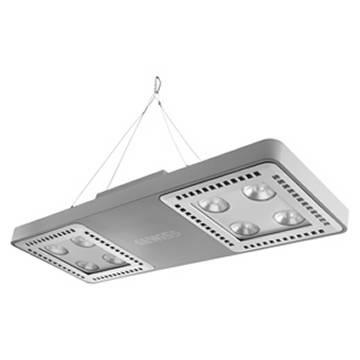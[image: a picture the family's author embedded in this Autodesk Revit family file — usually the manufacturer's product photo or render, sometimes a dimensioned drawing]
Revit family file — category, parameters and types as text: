
# Revit family: Lighting-Industriale-GEWISS-SMART[4]HE_APPARECCHI-LED_2M_DALI
name_source: partatom
category: Apparecchi per illuminazione
units: mm (PartAtom-declared; Revit-internal decimal feet)

## family parameters
Basato su piano di lavoro = Sì
Condiviso = No
Numero OmniClass = 23.80.70.00
Punto di calcolo locali = No
Quota connettore circolare = Usa diametro
Sempre verticale = No
Sorgente d'illuminazione = No
Taglio con vuoti quando caricato = No
Tipo di parte = Normale
Titolo OmniClass = Lighting

## types (1)
- Lighting-Industriale-GEWISS-SMART[4]HE_APPARECCHI-LED_2M_DALI
    Alimentatore = Incluso
    Apparecchio a ridotta temperatura superficiale = Si
    Applicazione = Interno
    Cablaggio = Con connettore stagno Gw connect
    Caratteristiche elettriche e gestione della luce = -
    Caratteristiche ottiche e illuminotecniche = -
    Carico apparente = 97 VA
    Catalogo = LIGHTING
    Certificazione DIN 18032-3 = Con Staffa - Kit Funi + morsetto (in approvazione)
    Certificazioni e classificazioni = -
    Classe fotobiologica = RG0
    Classe isolamento = I
    Classificazione = Lighting
    Classificazione: = -
    Codice Electrocod = 2444
    Codice digitale univoco (Datamatrix) = Datamatrix
    Colore = Grigio RAL 7035
    Commenti sul wattaggio = 97W
    Contesto = Illuminazione di industrie e impianti sportivi
    Controllo abbagliamento e luminanza = -
    Corpo = PA6 “Halogen Free” caricato fibra vetro
    Descrizione = SMART[4]HB 2M C.PAS.DALI ELL.57K
    Dispositivo di protezione = DM 6 kV / CM 10 kV
    Dist_sorg_lum = 10 mm  [stored 0.0328084 ft]
    Durata di vita = L90B10 (Tq+25°C) = 100.000 h - L90B10 (Tq+50°C) = 50.000 h
    Efficienza luminosa (lm/W) = 129
    Finitura colore = Grigio RAL 7035
    Fissaggio = -
    Frequenza nominale (Hz) = 50/60 Hz
    Gancio di chiusura = -
    Garanzia = 5 anni
    Grado di protezione = IP66
    Gruppo ottico = Riflettore in PC metallizzato e lenti in PMMA
    Guarnizioni = tipo siliconico antinvecchiamento
    IDF = ccb2858a-98df-48b0-bf72-33839f1a2588
    IDT = 32167967fdf74962832821affbd5ec12
    IPEA = -
    Immagine tipo = GWL1311.jpg
    Inclinazione = Con accessorio staffa
    Indice di resa cromatica = CRI-80
    Informazioni generali = -
    Installazione e manutenzione = -
    Lampada = LED
    Larghezza = 254 mm
    Lumen output (lm) = 12300
    Lunghezza = 699 mm  [stored 2.29331 ft]
    Mascherina = <Per categoria>
    Materiali = -
    Modello = GWS4223AQ857
    Motore = <Per categoria>
    Norma di riferimento = EN 60598-1 ; EN 60598-2-1 ; EN 60598-2-24
    Ottica = Ellittica
    Peso (kg): = 6,5
    Potenza di sistema = 95W
    Produttore = GEWISS S.p.A.
    Prospetto di default = 1219 mm
    Resistenza agli urti = IK08
    Resistenza al filo incandescente = 850 °C
    SEO = High bay
    Scheda Tecnica = https://www.gewiss.com
    Schermo = Vetro Temprato Spessore 4mm
    Sistema di controllo = 1 x DALI DT6
    Sistema di controllo : = DALI
    Sostituibilità gruppo ottico = Non sostituibile
    Sostituibilità piastra di cablaggio = Non sostituibile
    Spessore plafoniera = 40 mm  [stored 0.131234 ft]
    Struttura plafoniera = <Per categoria>
    Superficie massima esposta al vento : = 0,184 m²
    Temperatura di colore = 5700K
    Temperatura di esercizio = -30°C ÷ +50 °C
    Temperatura di stoccaggio = -40 +70 °C
    Tensione di alimentazione = 220 - 240 V
    Tipo di apparecchio = Riflettore industriale a LED&nbsp;
    Tipo di installazione e montaggio = Plafone - Parete - Sospensione
    Tipologia sorgente luminosa = LED - Non sostituibile
    Tolleranza cromatica = SDCM = 3
    Trasformatore = <Per categoria>
    URL = https://www.gewiss.com
    Vano di alimentazione = Integrato
    Versione file RFA = 20.11
    Viti esterne = Acciaio inox
    Voltaggio = 230 V

note: [stored X ft] marks values corroborated as IEEE doubles in the binary element streams (Revit-internal decimal feet)

## geometry (parser evidence)
native form markers: Blend x4, Sweep x3
no freeform markers — native parametric forms only
